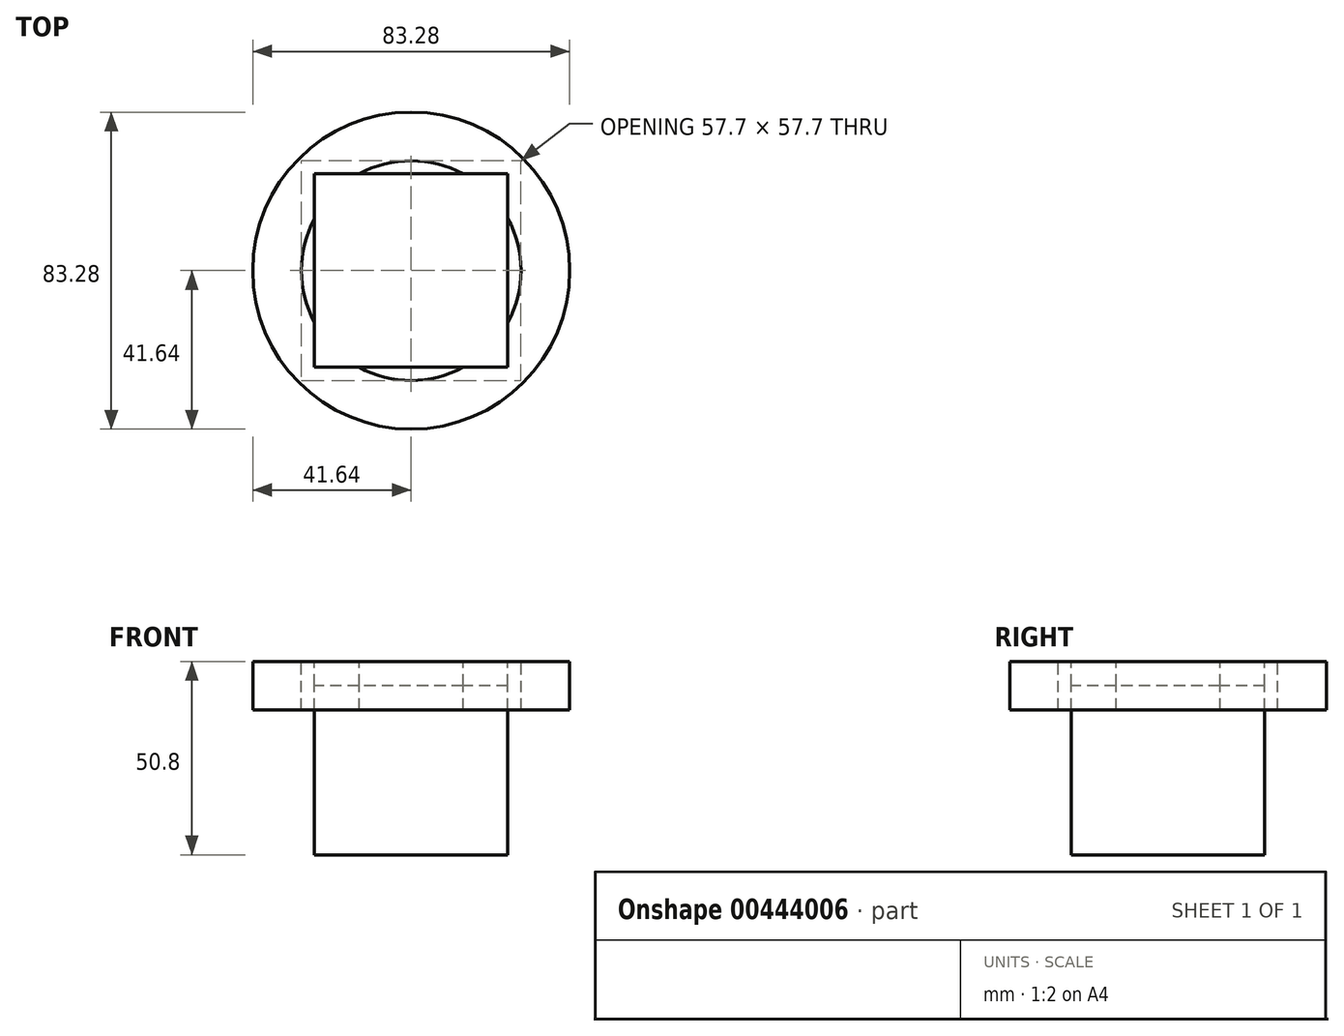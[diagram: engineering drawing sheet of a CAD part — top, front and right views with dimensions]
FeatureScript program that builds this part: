
annotation { "Feature Type Name" : "Feature", "Feature Type Description" : "" }
export const myFeature = defineFeature(function(context is Context, id is Id, definition is map)
    precondition{}
    {
        {
            var Q0;
            Q0=qCreatedBy(makeId("Top.planeOp"),FACE);
            var sketch = newSketch(context, id + "F0", { "sketchPlane" : qUnion([Q0])});
            skLineSegment(sketch, "E0.bottom", {"start": v(25.4, 25.4) * mm, "end": v(-25.4, 25.4) * mm});
            skLineSegment(sketch, "E0.top", {"start": v(25.4, -25.4) * mm, "end": v(-25.4, -25.4) * mm});
            skLineSegment(sketch, "E0.left", {"start": v(25.4, 25.4) * mm, "end": v(25.4, -25.4) * mm});
            skLineSegment(sketch, "E0.right", {"start": v(-25.4, 25.4) * mm, "end": v(-25.4, -25.4) * mm});
            skPoint(sketch, "E0.middle", {"position": v(0, 0) * mm});
            skSolve(sketch);
        }
        {
            var Q0;
            Q0 = qSketchRegion(id + "F0", true);
            extrude(context, id + "F1", {"entities" : qUnion([Q0]), "depth" : 44.45 * mm});
        }
        {
            var Q0;
            Q0=makeQuery(id+"F1.opExtrude","CAP_FACE",FACE,{"disambiguationData":[OSD([sQuery(id+"F0.wireOp",EDGE,"E0.bottom"),sQuery(id+"F0.wireOp",EDGE,"E0.top"),sQuery(id+"F0.wireOp",EDGE,"E0.left"),sQuery(id+"F0.wireOp",EDGE,"E0.right")])],"isStart":false});
            var sketch = newSketch(context, id + "F2", { "sketchPlane" : qUnion([Q0])});
            skCircle(sketch, "E1", {"center": v(0, 0) * mm, "radius": 28.85 * mm});
            skCircle(sketch, "E2", {"center": v(0, 0) * mm, "radius": 41.64 * mm});
            skSolve(sketch);
        }
        {
            var Q0;
            Q0=makeQuery(id+"F2.imprint","IMPRINT",FACE,{"disambiguationData":[TD([[makeQuery(id+"F2.imprint","IMPRINT",EDGE,{"derivedFrom":sQuery(id+"F2.wireOp",EDGE,"E2")}),1.0]])]});
            extrude(context, id + "F3", {"entities" : qUnion([Q0]), "operationType" : NewBodyOperationType.ADD, "oppositeDirection" : true, "depth" : 6.35 * mm, "hasSecondDirection" : true, "secondDirectionOppositeDirection" : false, "secondDirectionDepth" : 6.35 * mm});
        }
    });
